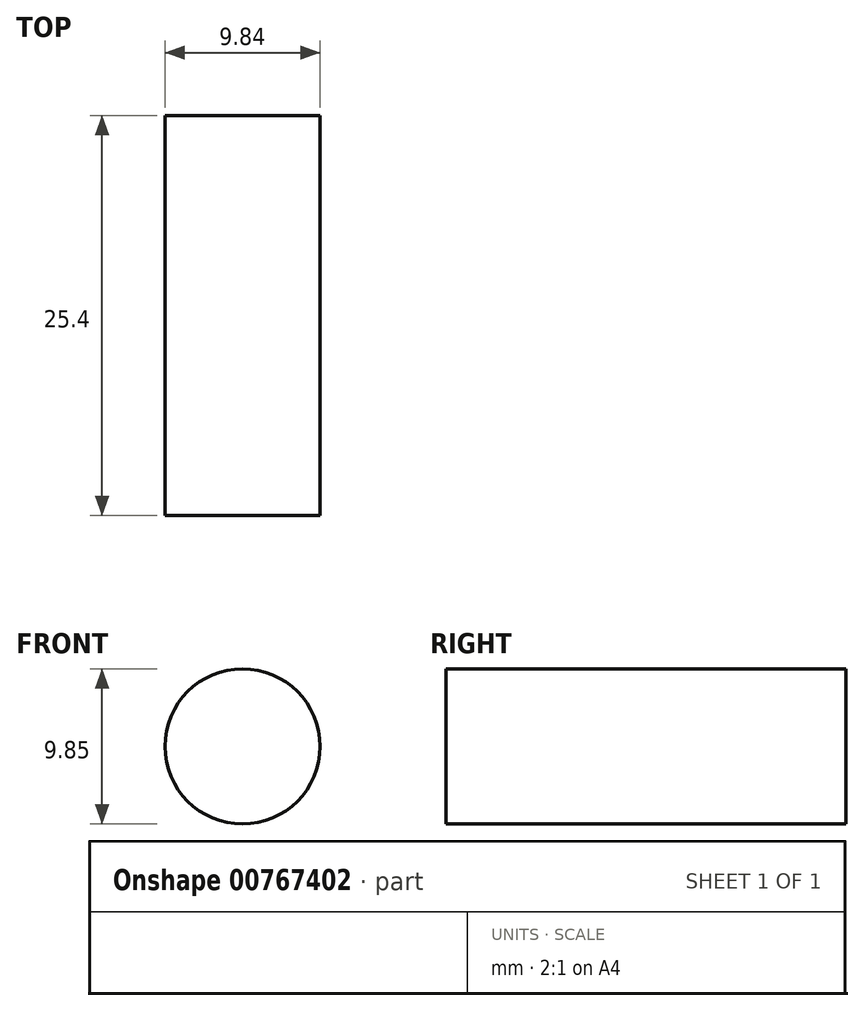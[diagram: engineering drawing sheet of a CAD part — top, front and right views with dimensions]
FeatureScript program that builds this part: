
annotation { "Feature Type Name" : "Feature", "Feature Type Description" : "" }
export const myFeature = defineFeature(function(context is Context, id is Id, definition is map)
    precondition{}
    {
        {
            var Q0;
            Q0=qCreatedBy(makeId("Front.planeOp"),FACE);
            var sketch = newSketch(context, id + "F0", { "sketchPlane" : qUnion([Q0])});
            skCircle(sketch, "E0", {"center": v(-5.74, 36.65) * mm, "radius": 49.8 * mm});
            skCircle(sketch, "E1", {"center": v(-5.74, 36.65) * mm, "radius": 4.92 * mm});
            skSolve(sketch);
        }
        {
            var Q0;
            Q0=makeQuery(id+"F0.imprint","IMPRINT",FACE,{"disambiguationData":[TD([[makeQuery(id+"F0.imprint","IMPRINT",EDGE,{"derivedFrom":sQuery(id+"F0.wireOp",EDGE,"E1")}),1.0]])]});
            extrude(context, id + "F1", {"entities" : qUnion([Q0]), "depth" : 25.4 * mm, "offsetDistance" : 25.4 * mm});
        }
    });
